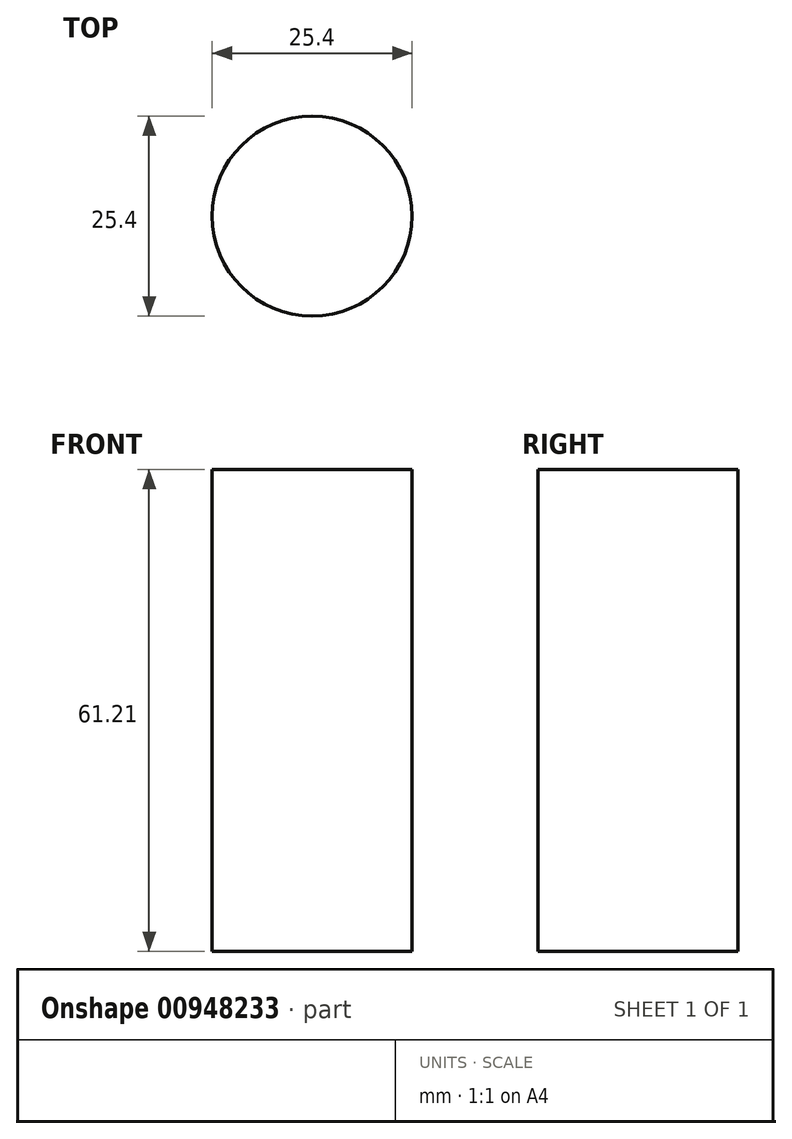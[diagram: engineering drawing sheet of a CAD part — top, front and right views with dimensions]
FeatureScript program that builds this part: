
annotation { "Feature Type Name" : "Feature", "Feature Type Description" : "" }
export const myFeature = defineFeature(function(context is Context, id is Id, definition is map)
    precondition{}
    {
        {
            var Q0;
            Q0=qCreatedBy(makeId("Top.planeOp"),FACE);
            var sketch = newSketch(context, id + "F0", { "sketchPlane" : qUnion([Q0])});
            skCircle(sketch, "E0", {"center": v(0, 0) * mm, "radius": 12.7 * mm});
            skSolve(sketch);
        }
        {
            var Q0;
            Q0=makeQuery(id+"F0.imprint","IMPRINT",FACE,{"disambiguationData":[TD([[makeQuery(id+"F0.imprint","IMPRINT",EDGE,{"derivedFrom":sQuery(id+"F0.wireOp",EDGE,"E0")}),1.0]])]});
            extrude(context, id + "F1", {"entities" : qUnion([Q0]), "depth" : 61.2 * mm, "offsetDistance" : 25.4 * mm});
        }
    });
